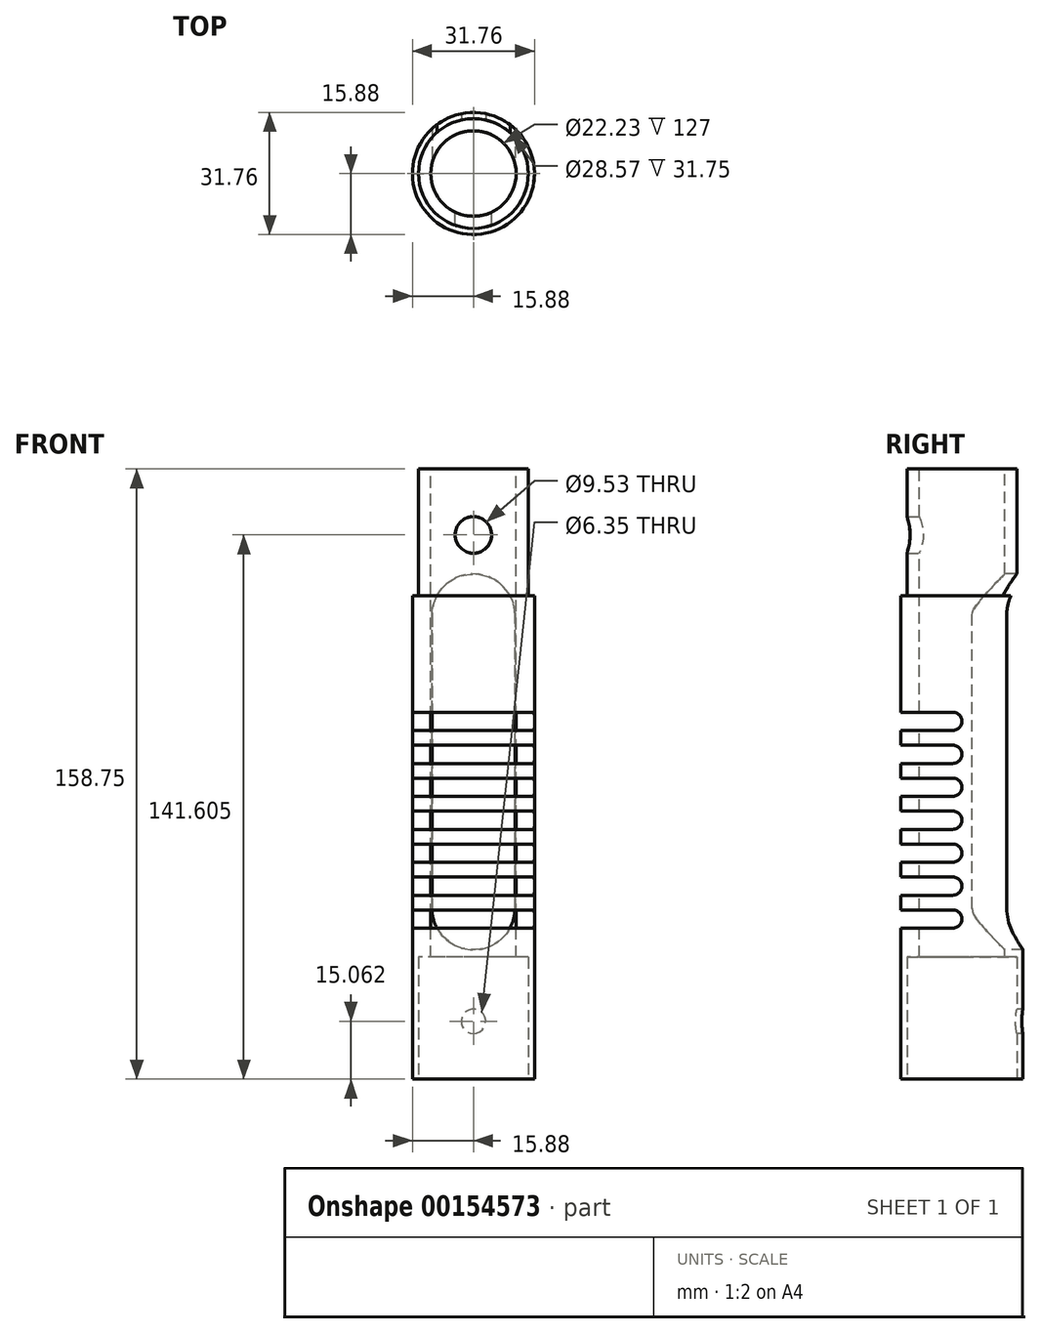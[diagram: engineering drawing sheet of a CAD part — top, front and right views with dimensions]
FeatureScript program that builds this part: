
annotation { "Feature Type Name" : "Feature", "Feature Type Description" : "" }
export const myFeature = defineFeature(function(context is Context, id is Id, definition is map)
    precondition{}
    {
        {
            var Q0;
            Q0=qCreatedBy(makeId("Top.planeOp"),FACE);
            var sketch = newSketch(context, id + "F0", { "sketchPlane" : qUnion([Q0])});
            skCircle(sketch, "E0", {"center": v(0, 0) * mm, "radius": 15.88 * mm});
            skSolve(sketch);
        }
        {
            var Q0;
            Q0 = qSketchRegion(id + "F0", true);
            extrude(context, id + "F1", {"entities" : qUnion([Q0]), "depth" : 158.75 * mm});
        }
        {
            var Q0;
            Q0=qCreatedBy(makeId("Right.planeOp"),FACE);
            var sketch = newSketch(context, id + "F2", { "sketchPlane" : qUnion([Q0])});
            skLineSegment(sketch, "E1", {"start": v(-38.36, 39.29) * mm, "end": v(-2.38, 39.29) * mm});
            skLineSegment(sketch, "E2", {"start": v(-38.36, 44.05) * mm, "end": v(-2.38, 44.05) * mm});
            skLineSegment(sketch, "E3", {"start": v(-2.38, 47.86) * mm, "end": v(-38.36, 47.86) * mm});
            skLineSegment(sketch, "E4", {"start": v(-38.36, 52.62) * mm, "end": v(-2.38, 52.62) * mm});
            skLineSegment(sketch, "E5", {"start": v(-2.38, 56.43) * mm, "end": v(-38.36, 56.43) * mm});
            skLineSegment(sketch, "E6", {"start": v(-38.36, 61.2) * mm, "end": v(-2.38, 61.2) * mm});
            skLineSegment(sketch, "E7", {"start": v(-2.38, 65) * mm, "end": v(-38.36, 65) * mm});
            skLineSegment(sketch, "E8", {"start": v(-38.36, 69.77) * mm, "end": v(-2.38, 69.77) * mm});
            skLineSegment(sketch, "E9", {"start": v(-2.38, 73.58) * mm, "end": v(-38.36, 73.58) * mm});
            skLineSegment(sketch, "E10", {"start": v(-38.36, 78.34) * mm, "end": v(-2.38, 78.34) * mm});
            skLineSegment(sketch, "E11", {"start": v(-2.38, 82.15) * mm, "end": v(-38.36, 82.15) * mm});
            skLineSegment(sketch, "E12", {"start": v(-38.36, 86.91) * mm, "end": v(-2.38, 86.91) * mm});
            skLineSegment(sketch, "E13", {"start": v(-2.38, 90.72) * mm, "end": v(-38.36, 90.72) * mm});
            skLineSegment(sketch, "E14", {"start": v(-38.36, 95.49) * mm, "end": v(-2.38, 95.49) * mm});
            skArc(sketch, "E15", {"start": v(-2.38, 39.29) * mm, "mid": v(0, 41.67) * mm, "end": v(-2.38, 44.05) * mm});
            skArc(sketch, "E16", {"start": v(-2.38, 47.86) * mm, "mid": v(0, 50.24) * mm, "end": v(-2.38, 52.62) * mm});
            skArc(sketch, "E17", {"start": v(-2.38, 56.43) * mm, "mid": v(0, 58.81) * mm, "end": v(-2.38, 61.2) * mm});
            skArc(sketch, "E18", {"start": v(-2.38, 65) * mm, "mid": v(0, 67.39) * mm, "end": v(-2.38, 69.77) * mm});
            skArc(sketch, "E19", {"start": v(-2.38, 73.58) * mm, "mid": v(0, 75.96) * mm, "end": v(-2.38, 78.34) * mm});
            skArc(sketch, "E20", {"start": v(-2.38, 82.15) * mm, "mid": v(0, 84.53) * mm, "end": v(-2.38, 86.91) * mm});
            skArc(sketch, "E21", {"start": v(-2.38, 90.72) * mm, "mid": v(0, 93.1) * mm, "end": v(-2.38, 95.49) * mm});
            skLineSegment(sketch, "E22", {"start": v(-38.36, 39.29) * mm, "end": v(-38.36, 44.05) * mm});
            skLineSegment(sketch, "E23", {"start": v(-38.36, 47.86) * mm, "end": v(-38.36, 52.62) * mm});
            skLineSegment(sketch, "E24", {"start": v(-38.36, 56.43) * mm, "end": v(-38.36, 61.2) * mm});
            skLineSegment(sketch, "E25", {"start": v(-38.36, 65) * mm, "end": v(-38.36, 69.77) * mm});
            skLineSegment(sketch, "E26", {"start": v(-38.36, 73.58) * mm, "end": v(-38.36, 78.34) * mm});
            skLineSegment(sketch, "E27", {"start": v(-38.36, 82.15) * mm, "end": v(-38.36, 86.91) * mm});
            skLineSegment(sketch, "E28", {"start": v(-38.36, 90.72) * mm, "end": v(-38.36, 95.49) * mm});
            skSolve(sketch);
        }
        {
            var Q0;
            Q0 = qSketchRegion(id + "F2", true);
            extrude(context, id + "F3", {"entities" : qUnion([Q0]), "operationType" : NewBodyOperationType.REMOVE, "endBound" : BoundingType.SYMMETRIC, "oppositeDirection" : true, "depth" : 50.8 * mm});
        }
        {
            var Q0;
            Q0=qCreatedBy(makeId("Top.planeOp"),FACE);
            var sketch = newSketch(context, id + "F4", { "sketchPlane" : qUnion([Q0])});
            skCircle(sketch, "E29", {"center": v(0, 0) * mm, "radius": 14.29 * mm});
            skSolve(sketch);
        }
        {
            var Q0;
            Q0 = qSketchRegion(id + "F4", true);
            extrude(context, id + "F5", {"entities" : qUnion([Q0]), "operationType" : NewBodyOperationType.REMOVE, "depth" : 31.75 * mm});
        }
        {
            var Q0;
            Q0=makeQuery(id+"F1.opExtrude","CAP_FACE",FACE,{"disambiguationData":[OSD([sQuery(id+"F0.wireOp",EDGE,"E0")])],"isStart":false});
            var sketch = newSketch(context, id + "F6", { "sketchPlane" : qUnion([Q0])});
            skCircle(sketch, "E30", {"center": v(0, 0) * mm, "radius": 11.11 * mm});
            skSolve(sketch);
        }
        {
            var Q0;
            Q0 = qSketchRegion(id + "F6", true);
            extrude(context, id + "F7", {"entities" : qUnion([Q0]), "operationType" : NewBodyOperationType.REMOVE, "endBound" : BoundingType.THROUGH_ALL, "oppositeDirection" : true, "depth" : 25.4 * mm});
        }
        {
            var Q0;
            Q0=qCreatedBy(makeId("Front.planeOp"),FACE);
            var sketch = newSketch(context, id + "F8", { "sketchPlane" : qUnion([Q0])});
            skLineSegment(sketch, "E31", {"start": v(10.8, 120.65) * mm, "end": v(10.8, 44.45) * mm});
            skLineSegment(sketch, "E32", {"start": v(-10.8, 44.45) * mm, "end": v(-10.8, 120.65) * mm});
            skArc(sketch, "E33", {"start": v(10.8, 44.45) * mm, "mid": v(0, 33.66) * mm, "end": v(-10.8, 44.45) * mm});
            skArc(sketch, "E34", {"start": v(10.8, 120.65) * mm, "mid": v(0, 131.44) * mm, "end": v(-10.8, 120.65) * mm});
            skSolve(sketch);
        }
        {
            var Q0;
            Q0 = qSketchRegion(id + "F8", true);
            var Q1;
            Q1 = qConstructionFilter(qBodyType(qCreatedBy(id + "F8" ,EDGE), BodyType.WIRE), ConstructionObject.NO);
            var Q2;
            Q2=makeQuery(id+"F1.opExtrude","SWEPT_FACE",FACE,{"disambiguationData":[OSD([sQuery(id+"F0.wireOp",EDGE,"E0")])]});
            extrude(context, id + "F9", {"entities" : qUnion([Q0]), "operationType" : NewBodyOperationType.REMOVE, "surfaceEntities" : qUnion([Q1]), "endBound" : BoundingType.THROUGH_ALL, "oppositeDirection" : true, "endBoundEntityFace" : qUnion([Q2]), "depth" : 50.8 * mm});
        }
        {
            var Q0;
            Q0=makeQuery(id+"F1.opExtrude","CAP_FACE",FACE,{"disambiguationData":[OSD([sQuery(id+"F0.wireOp",EDGE,"E0")])],"isStart":false});
            var sketch = newSketch(context, id + "F10", { "sketchPlane" : qUnion([Q0])});
            skCircle(sketch, "E35", {"center": v(0, 0) * mm, "radius": 19.05 * mm});
            skCircle(sketch, "E36", {"center": v(0, 0) * mm, "radius": 14.29 * mm});
            skSolve(sketch);
        }
        {
            var Q0;
            Q0 = qSketchRegion(id + "F10", true);
            extrude(context, id + "F11", {"entities" : qUnion([Q0]), "operationType" : NewBodyOperationType.REMOVE, "oppositeDirection" : true, "depth" : 33.02 * mm});
        }
        {
            var Q0;
            Q0=qCreatedBy(makeId("Front.planeOp"),FACE);
            var sketch = newSketch(context, id + "F12", { "sketchPlane" : qUnion([Q0])});
            skCircle(sketch, "E37", {"center": v(0, 141.6) * mm, "radius": 4.76 * mm});
            skSolve(sketch);
        }
        {
            var Q0;
            Q0 = qSketchRegion(id + "F12", true);
            extrude(context, id + "F13", {"entities" : qUnion([Q0]), "operationType" : NewBodyOperationType.REMOVE, "endBound" : BoundingType.THROUGH_ALL, "depth" : 25.4 * mm});
        }
        {
            var Q0;
            Q0=qCreatedBy(makeId("Front.planeOp"),FACE);
            var sketch = newSketch(context, id + "F14", { "sketchPlane" : qUnion([Q0])});
            skCircle(sketch, "E38", {"center": v(0, 15.06) * mm, "radius": 3.18 * mm});
            skSolve(sketch);
        }
        {
            var Q0;
            Q0 = qSketchRegion(id + "F14", true);
            extrude(context, id + "F15", {"entities" : qUnion([Q0]), "operationType" : NewBodyOperationType.REMOVE, "endBound" : BoundingType.THROUGH_ALL, "oppositeDirection" : true, "depth" : 25.4 * mm});
        }
    });
